# Revit family: Specialty_Equipment-Fiberstone_Planter-Stone_Yard-Zaragoza-Round
name_source: partatom
category: Specialty Equipment
units: mm (PartAtom-declared; Revit-internal decimal feet)

## family parameters
Always vertical = Yes
Cut with Voids When Loaded = No
Enable Cutting in Views = No
Maintain Annotation Orientation = No
OmniClass Number = 23.40.05.21.17
OmniClass Title = Planters
Part Type = Normal
Room Calculation Point = No
Round Connector Dimension = Use Diameter
Shared = No
Work Plane-Based = No

## types (16) — shared parameters
Assembly Code = G2050600
CD_Finish = Concrete-Fiberstone-Carlsbad-Chalk
CD_Microsite = https://www.caddetails.com
CD_Pad Size = 3.0"
CD_Product Page URL = https://stoneyardinc.com
CD_Specification = https://stoneyardinc.com
Default Elevation = 0.0"
Description = Zaragoza Planters
Manufacturer = Stone Yard
Model = Zaragoza Planter
Type Comments = Round Planter
URL = https://stoneyardinc.com

## per-type parameters (varying)
| type | CD_Diameter | CD_Diameter Baseplate | CD_Diameter Lip | CD_Height |
| 10.5"Dia x 16"H | 10.5" | 5.3" | 6.5" | 16.0" |
| 16"Dia x 24"H | 16.0" | 8.0" | 12.0" | 24.0" |
| 16.5"Dia x 36"H | 16.5" | 8.3" | 12.5" | 36.0" |
| 20"Dia x 17"H | 20.0" | 10.0" | 16.0" | 17.0" |
| 21"Dia x 30"H | 21.0" | 10.5" | 17.0" | 30.0" |
| 22"Dia x 18"H | 22.0" | 11.0" | 18.0" | 18.0" |
| 26"Dia x 14.5"H | 26.0" | 13.0" | 22.0" | 14.5" |
| 27"Dia x 23"H | 27.0" | 13.5" | 23.0" | 23.0" |
| 27"Dia x 30"H | 27.0" | 13.5" | 23.0" | 30.0" |
| 28"Dia x 46"H | 28.0" | 14.0" | 24.0" | 46.0" |
| 30"Dia x 36"H | 30.0" | 15.0" | 26.0" | 36.0" |
| 33"Dia x 60"H | 33.0" | 16.5" | 29.0" | 60.0" |
| 36"Dia x 20"H | 36.0" | 18.0" | 32.0" | 20.0" |
| 36"Dia x 28"H | 36.0" | 18.0" | 32.0" | 28.0" |
| 43"Dia x 46"H | 43.0" | 21.5" | 39.0" | 46.0" |
| 60"Dia x 38"H | 60.0" | 30.0" | 56.0" | 38.0" |

## geometry (parser evidence)
native form markers: Sweep x3
no freeform markers — native parametric forms only
